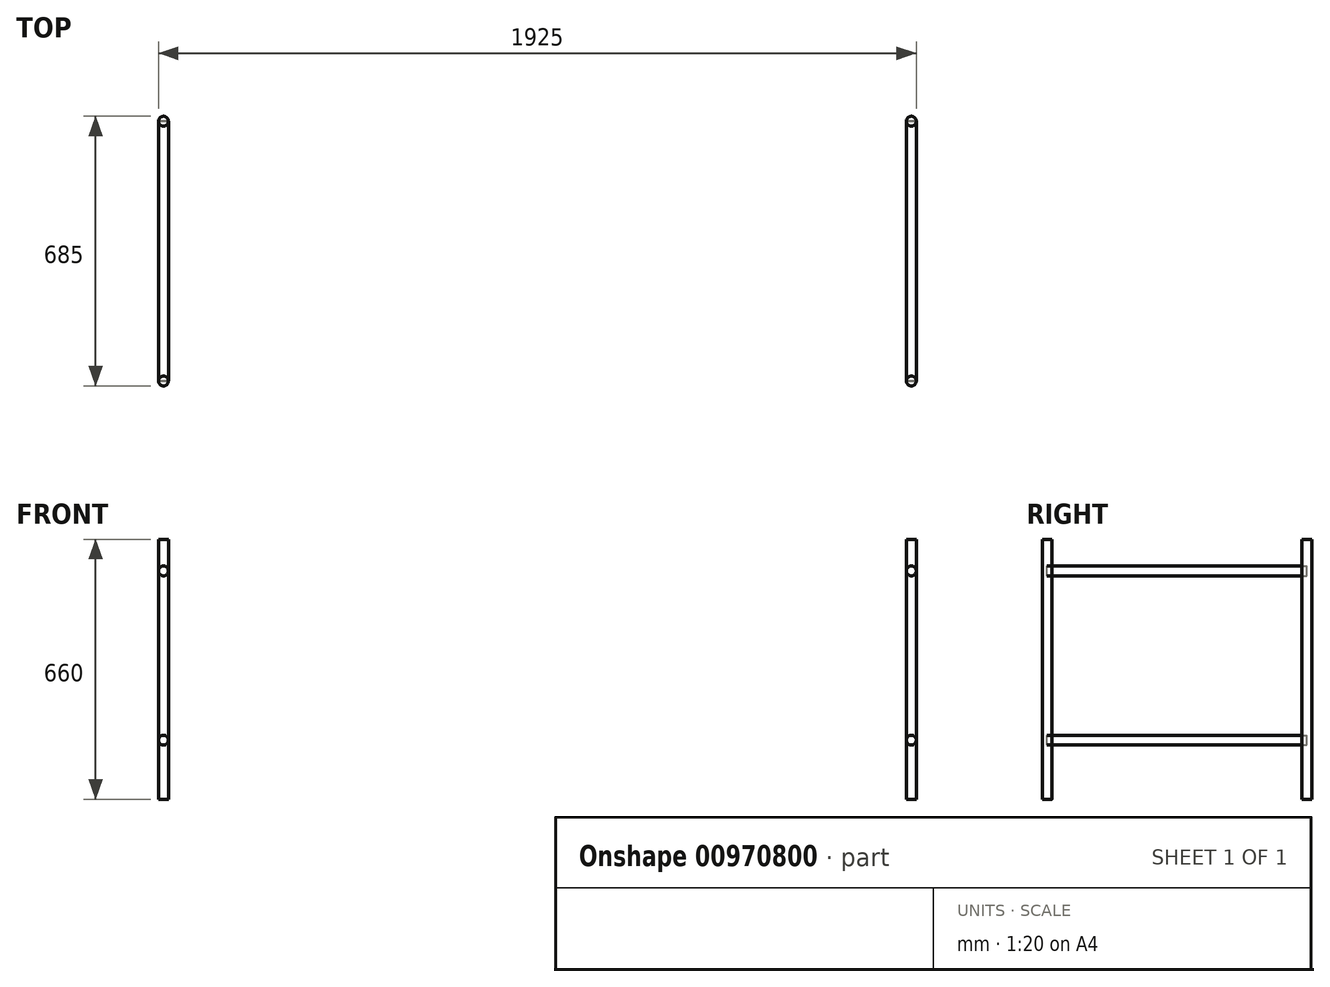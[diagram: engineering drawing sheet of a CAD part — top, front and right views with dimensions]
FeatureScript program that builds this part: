
annotation { "Feature Type Name" : "Feature", "Feature Type Description" : "" }
export const myFeature = defineFeature(function(context is Context, id is Id, definition is map)
    precondition{}
    {
        {
            var Q0;
            Q0=qCreatedBy(makeId("Top.planeOp"),FACE);
            var sketch = newSketch(context, id + "F0", { "sketchPlane" : qUnion([Q0])});
            skLineSegment(sketch, "E0.bottom", {"start": v(-950, -660) * mm, "end": v(950, -660) * mm, "construction": true});
            skLineSegment(sketch, "E0.top", {"start": v(-950, 0) * mm, "end": v(950, 0) * mm, "construction": true});
            skLineSegment(sketch, "E0.left", {"start": v(-950, -660) * mm, "end": v(-950, 0) * mm, "construction": true});
            skLineSegment(sketch, "E0.right", {"start": v(950, -660) * mm, "end": v(950, 0) * mm, "construction": true});
            skCircle(sketch, "E1", {"center": v(-950, 0) * mm, "radius": 12.5 * mm});
            skCircle(sketch, "E2", {"center": v(-950, -660) * mm, "radius": 12.5 * mm});
            skCircle(sketch, "E3", {"center": v(950, -660) * mm, "radius": 12.5 * mm});
            skCircle(sketch, "E4", {"center": v(950, 0) * mm, "radius": 12.5 * mm});
            skSolve(sketch);
        }
        {
            var Q0;
            Q0=qSketchRegion(id+"F0",true);
            extrude(context, id + "F1", {"entities" : qUnion([Q0]), "depth" : 660 * mm, "offsetDistance" : 25 * mm});
        }
        {
            var Q0;
            Q0=qCreatedBy(makeId("Front.planeOp"),FACE);
            var sketch = newSketch(context, id + "F2", { "sketchPlane" : qUnion([Q0])});
            skLineSegment(sketch, "E5.bottom", {"start": v(-950, 0) * mm, "end": v(950, 0) * mm, "construction": true});
            skLineSegment(sketch, "E5.top", {"start": v(-950, 580) * mm, "end": v(950, 580) * mm, "construction": true});
            skLineSegment(sketch, "E5.left", {"start": v(-950, 0) * mm, "end": v(-950, 580) * mm, "construction": true});
            skLineSegment(sketch, "E5.right", {"start": v(950, 0) * mm, "end": v(950, 580) * mm, "construction": true});
            skLineSegment(sketch, "E6", {"start": v(-950, 150) * mm, "end": v(950, 150) * mm, "construction": true});
            skCircle(sketch, "E7", {"center": v(-950, 580) * mm, "radius": 12.5 * mm});
            skCircle(sketch, "E8", {"center": v(-950, 150) * mm, "radius": 12.5 * mm});
            skCircle(sketch, "E9", {"center": v(950, 580) * mm, "radius": 12.5 * mm});
            skCircle(sketch, "E10", {"center": v(950, 150) * mm, "radius": 12.5 * mm});
            skSolve(sketch);
        }
        {
            var Q0;
            Q0=qSketchRegion(id+"F2",true);
            extrude(context, id + "F3", {"entities" : qUnion([Q0]), "depth" : 660 * mm, "offsetDistance" : 25 * mm});
        }
    });
